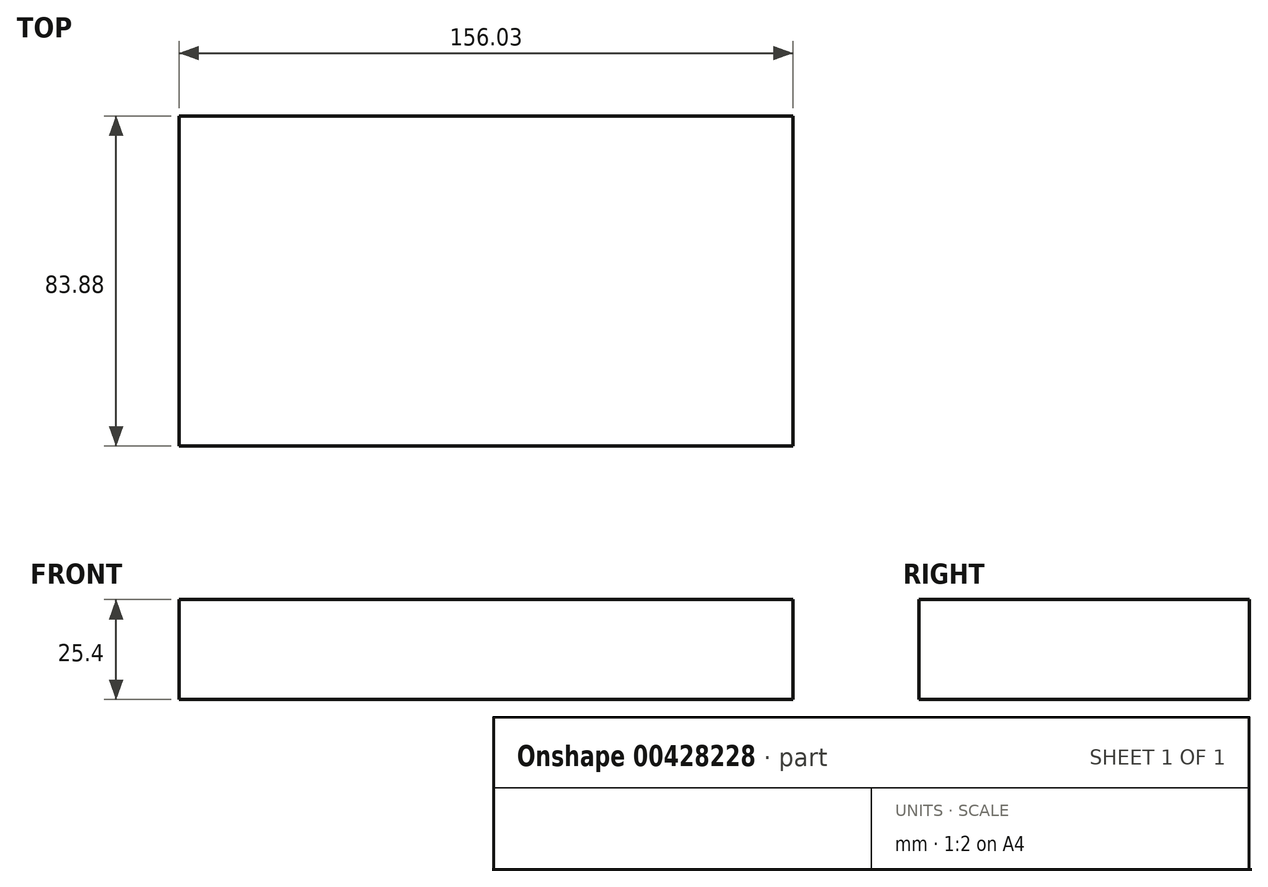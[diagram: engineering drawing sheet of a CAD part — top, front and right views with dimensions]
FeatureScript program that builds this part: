
annotation { "Feature Type Name" : "Feature", "Feature Type Description" : "" }
export const myFeature = defineFeature(function(context is Context, id is Id, definition is map)
    precondition{}
    {
        {
            var Q0;
            Q0=qCreatedBy(makeId("Top.planeOp"),FACE);
            var sketch = newSketch(context, id + "F0", { "sketchPlane" : qUnion([Q0])});
            skLineSegment(sketch, "E0.bottom", {"start": v(-114.11, 0) * mm, "end": v(41.92, 0) * mm});
            skLineSegment(sketch, "E0.top", {"start": v(-114.11, -83.88) * mm, "end": v(41.92, -83.88) * mm});
            skLineSegment(sketch, "E0.left", {"start": v(-114.11, 0) * mm, "end": v(-114.11, -83.88) * mm});
            skLineSegment(sketch, "E0.right", {"start": v(41.92, 0) * mm, "end": v(41.92, -83.88) * mm});
            skSolve(sketch);
        }
        {
            var Q0;
            Q0=makeQuery(id+"F0.imprint","IMPRINT",FACE,{"disambiguationData":[TD([[makeQuery(id+"F0.imprint","IMPRINT",EDGE,{"derivedFrom":sQuery(id+"F0.wireOp",EDGE,"E0.bottom")}),-1.0]])]});
            extrude(context, id + "F1", {"entities" : qUnion([Q0]), "depth" : 25.4 * mm});
        }
    });
